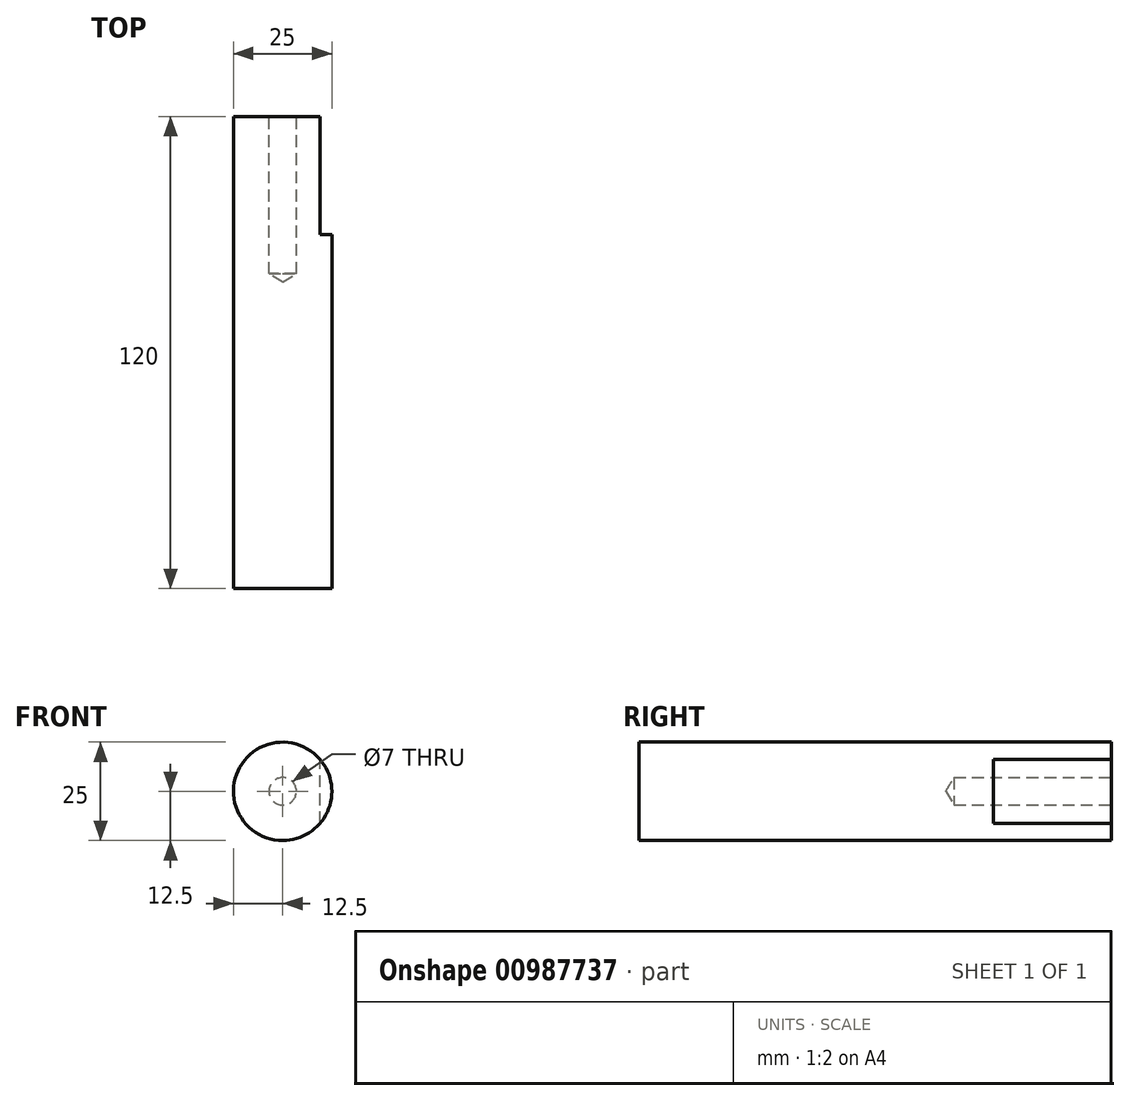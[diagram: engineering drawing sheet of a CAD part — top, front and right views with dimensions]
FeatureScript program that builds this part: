
annotation { "Feature Type Name" : "Feature", "Feature Type Description" : "" }
export const myFeature = defineFeature(function(context is Context, id is Id, definition is map)
    precondition{}
    {
        {
            var Q0;
            Q0=qCreatedBy(makeId("Front.planeOp"),FACE);
            var sketch = newSketch(context, id + "F0", { "sketchPlane" : qUnion([Q0])});
            skCircle(sketch, "E0", {"center": v(0, 0) * mm, "radius": 12.5 * mm});
            skSolve(sketch);
        }
        {
            var Q0;
            Q0 = qSketchRegion(id + "F0", true);
            extrude(context, id + "F1", {"entities" : qUnion([Q0]), "depth" : 120 * mm, "offsetDistance" : 25 * mm});
        }
        {
            var Q0;
            Q0=makeQuery(id+"F1.opExtrude","CAP_FACE",FACE,{"disambiguationData":[OSD([sQuery(id+"F0.wireOp",EDGE,"E0")])],"isStart":true});
            var sketch = newSketch(context, id + "F2", { "sketchPlane" : qUnion([Q0])});
            skPoint(sketch, "E1", {"position": v(0, 0) * mm});
            skSolve(sketch);
        }
        {
            var Q0;
            Q0=sQuery(id+"F2.wireOp",VERTEX,"E1");
            var Q1;
            Q1=makeQuery(id+"F1.opExtrude","SWEPT_BODY",BODY,{"disambiguationData":[OSD([sQuery(id+"F0.wireOp",EDGE,"E0")])]});
            hole(context, id + "F3", {"style" : HoleStyle.SIMPLE, "endStyle" : HoleEndStyle.BLIND, "standardTappedOrClearance" : lookupTablePath({ "standard" : "ISO", "size" : "7", "type" : "Drilled" }), "standardBlindInLast" : lookupTablePath({ "standard" : "ISO", "size" : "7", "type" : "Drilled" }), "holeDiameter" : 7 * mm, "majorDiameter" : 8 * mm, "holeDepth" : 40 * mm, "isTappedThrough" : true, "tappedDepth" : 11.6 * mm, "tapClearance" : 3, "startFromSketch" : true, "locations" : qUnion([Q0]), "scope" : qUnion([Q1])});
        }
        {
            var Q0;
            Q0=qCreatedBy(makeId("Right.planeOp"),FACE);
            cPlane(context, id + "F4", {"entities" : qUnion([Q0]), "cplaneType" : CPlaneType.OFFSET, "offset" : 12.5 * mm, "width" : 150 * mm, "height" : 150 * mm});
        }
        {
            var Q0;
            Q0=qCreatedBy(id+"F4.planeOp",FACE);
            var sketch = newSketch(context, id + "F5", { "sketchPlane" : qUnion([Q0])});
            skLineSegment(sketch, "E2.bottom", {"start": v(0, -15.57) * mm, "end": v(-30, -15.57) * mm});
            skLineSegment(sketch, "E2.top", {"start": v(0, 15.07) * mm, "end": v(-30, 15.07) * mm});
            skLineSegment(sketch, "E2.left", {"start": v(0, -15.57) * mm, "end": v(0, 15.07) * mm});
            skLineSegment(sketch, "E2.right", {"start": v(-30, -15.57) * mm, "end": v(-30, 15.07) * mm});
            skSolve(sketch);
        }
        {
            var Q0;
            Q0 = qSketchRegion(id + "F5", true);
            extrude(context, id + "F6", {"entities" : qUnion([Q0]), "operationType" : NewBodyOperationType.REMOVE, "oppositeDirection" : true, "depth" : 3 * mm, "offsetDistance" : 25 * mm});
        }
    });
